# Revit family: Fireclass_Addressable Base Sounder_Visual Indicator Devices
name_source: partatom
category: Fire Alarm Devices
revit_build: Autodesk Revit 2014 (Build: 20130308_1515(x64)
units: mm (PartAtom-declared; Revit-internal decimal feet)

## types (3) — shared parameters
Asset Type = Moveable
Brand = FireClass
Duration Unit = Year
Finish = TBC
Has Protective Earth = No
Ifc Export As = TBC
Ifc Export Type = TBC
Ifc Type Object = IfcBuildingElementProxy
Installation Date = TBC
Manufacturer = Tyco Fire Protection Products
Manufacturer Name = Tyco Fire Protection Products
Manufacturer URL = www.fireclass.co.uk
Material = TBC
Nominal  Diameter = 114 mm
Nominal Height = 45 mm
Nominal Length = 114 mm
Nominal Voltage = 40 V DC
Nominal Width = 114 mm
Operation Temperature Range = -25 to +70
Product Information = TBC
Relative Humidity = Up to 95% non-condensing
Shape = Circular
Storage Temperature = -25 to +70
URL = TBC
Version = 1
Voltage = 20V-40V, 35V nominal
Warranty Duration Labor = 3 years
Warranty Duration Parts = 3 years (TBC)
Warranty Duration Unit = Year
Warranty Start Date = TBC

## per-type parameters (varying)
| type | Alarm Current | BIM Object Name | Category | Colour | Description | Electrical Device Nominal Power | Features | LED | LED Colour | Model | Model Reference | NBS Description | NBS Reference | Name | Nominal Current | Product Codes | Product Specification | Quiescent Current | Short Circuit Isolators | Uniclass2 | Weight |
| Fireclass Addressable Base Sounder | 400uA | Tyco_FireDtctnAlmCtrlIndctEquip_FireClass Addressable Base Sounder-FC440SB | Pr_70_75_02_30 | White | FC440SB FireClass Addressable Base Sounder | 160mW | FireClass Addressable Base Sounder | No | White | FC440SB | FC440SB FireClass Addressable Base Sounder | Fire Alarm Sounders | 90-75-30/360 | FC440SB Addressable Base Sdr | 1.1A | 576.440.002 | FC440SB FireClass Addressable Base Sounder | 4mA | Yes | Pr_70_75_02_30 | 161g |
| Fireclass Detector Base Sounder | 100uA | Tyco_FireDtctnAlmCtrlIndctEquip_Fireclass-Detector Base Sounder-FC440DSB | Pr_70_75_02_30 | White | FC440DSB FireClass Detector Base Sounder | 160mW | FireClass Detector Base Sounder | No | White | FC440DSB | FC440DSB FireClass Detector Base Sounder | Fire Alarm Sounders | 90-75-30/360 | FC440DSB Detector Base Sounder |  | 576.440.001 | FC440DSB FireClass Detector Base Sounder | 4mA | No | Pr_70_75_02_30 | 161g |
| Fireclass Addressable Base Sounder Beacon VID | 400uA | Tyco_FireDtctnAlmCtrlIndctEquip_FireClass-Addressable Base Sounder Beacon Visual Indicating Device Red LEDs-FC440AIB | Pr_70_75_02_97 | Transluscent | FC440AIB FireClass Addressable Base Sounder Beacon Visual Indicating Device Red LEDs | 320mW | FireClass Addressable Base Sounder Beacon Visual Indicating Device Red LEDs | Yes | Red | FC440AIB | FC440AIB FireClass Addressable Base Sounder Beacon Visual Indicating Device Red LEDs | Visual Alarm Signal Devices | 90-75-30/415 | FC440AIB Add Base Sounder VID | 1.1A | 576.440.010 | FC440AIB Zettler Addressable Base Sounder Beacon VID | 8mA | Yes | Pr_70_75_02_97 | 167g |

## geometry (parser evidence)
native form markers: Sweep x7
no freeform markers — native parametric forms only
